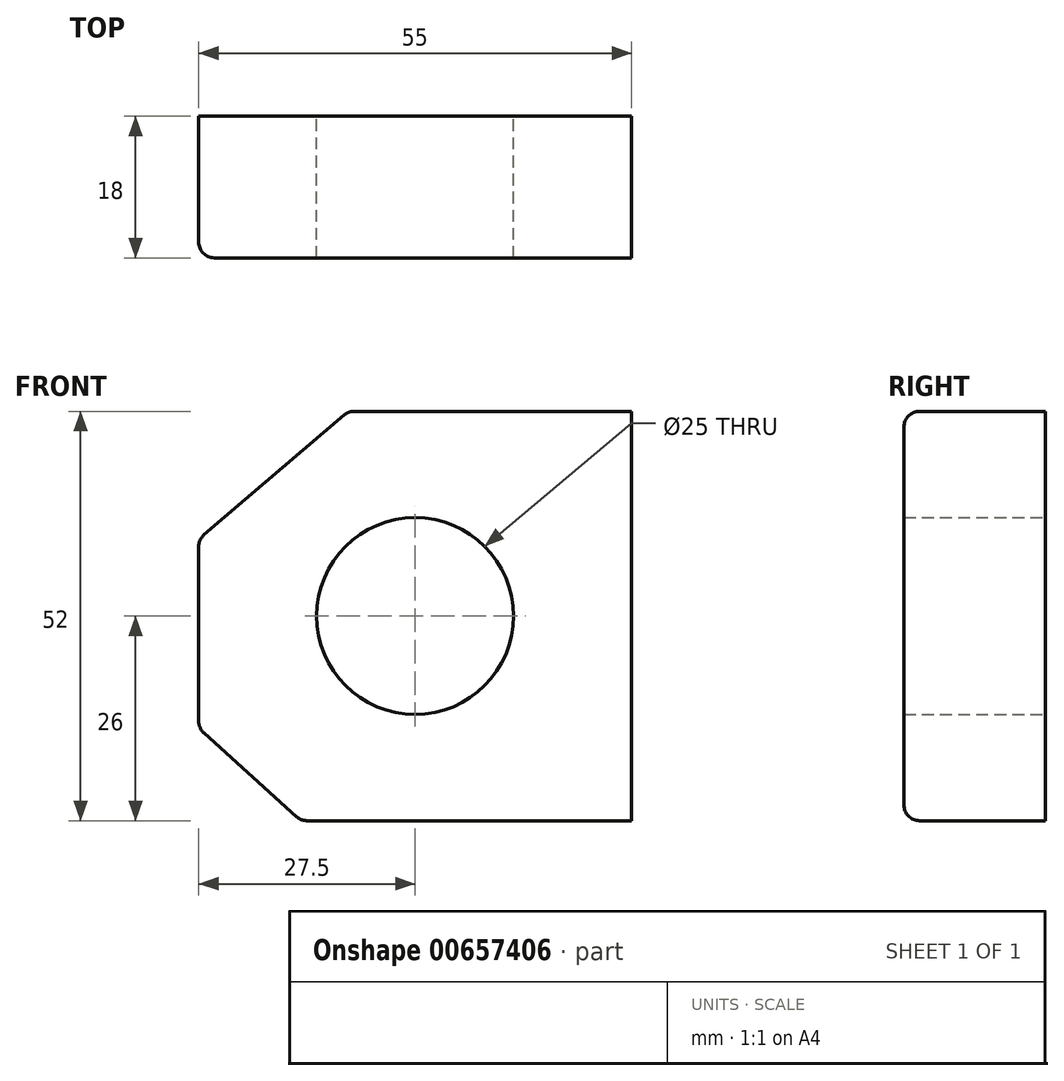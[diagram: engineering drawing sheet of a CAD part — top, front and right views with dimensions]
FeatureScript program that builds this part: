
annotation { "Feature Type Name" : "Feature", "Feature Type Description" : "" }
export const myFeature = defineFeature(function(context is Context, id is Id, definition is map)
    precondition{}
    {
        {
            var Q0;
            Q0=qCreatedBy(makeId("Front.planeOp"),FACE);
            var sketch = newSketch(context, id + "F0", { "sketchPlane" : qUnion([Q0])});
            skLineSegment(sketch, "E0.bottom", {"start": v(27.5, -26) * mm, "end": v(-14.5, -26) * mm});
            skLineSegment(sketch, "E0.top", {"start": v(27.5, 26) * mm, "end": v(-8.5, 26) * mm});
            skLineSegment(sketch, "E0.left", {"start": v(27.5, -26) * mm, "end": v(27.5, 26) * mm});
            skLineSegment(sketch, "E0.right", {"start": v(-27.5, -14.25) * mm, "end": v(-27.5, 9.75) * mm});
            skPoint(sketch, "E0.middle", {"position": v(0, 0) * mm});
            skLineSegment(sketch, "E1", {"start": v(-8.5, 26) * mm, "end": v(-27.5, 9.75) * mm});
            skPoint(sketch, "E2.orphan", {"position": v(-27.5, 26) * mm});
            skLineSegment(sketch, "E3", {"start": v(-27.5, -14.25) * mm, "end": v(-14.5, -26) * mm});
            skPoint(sketch, "E4.orphan", {"position": v(-27.5, -26) * mm});
            skCircle(sketch, "E5", {"center": v(0, 0) * mm, "radius": 12.5 * mm});
            skSolve(sketch);
        }
        {
            var Q0;
            Q0=makeQuery(id+"F0.imprint","IMPRINT",FACE,{"disambiguationData":[TD([[makeQuery(id+"F0.imprint","IMPRINT",EDGE,{"derivedFrom":sQuery(id+"F0.wireOp",EDGE,"E0.bottom")}),-1.0]])]});
            extrude(context, id + "F1", {"entities" : qUnion([Q0]), "endBound" : BoundingType.SYMMETRIC, "depth" : 18 * mm, "offsetDistance" : 25 * mm});
        }
        {
            var Q0;
            Q0=makeQuery(id+"F1.opExtrude","CAP_EDGE",EDGE,{"disambiguationData":[OSD([sQuery(id+"F0.wireOp",EDGE,"E0.top")])],"isStart":false});
            var Q1;
            Q1=makeQuery(id+"F1.opExtrude","CAP_EDGE",EDGE,{"disambiguationData":[OSD([sQuery(id+"F0.wireOp",EDGE,"E1")])],"isStart":false});
            var Q2;
            Q2=makeQuery(id+"F1.opExtrude","CAP_EDGE",EDGE,{"disambiguationData":[OSD([sQuery(id+"F0.wireOp",EDGE,"E0.right")])],"isStart":false});
            var Q3;
            Q3=makeQuery(id+"F1.opExtrude","CAP_EDGE",EDGE,{"disambiguationData":[OSD([sQuery(id+"F0.wireOp",EDGE,"E3")])],"isStart":false});
            var Q4;
            Q4=makeQuery(id+"F1.opExtrude","CAP_EDGE",EDGE,{"disambiguationData":[OSD([sQuery(id+"F0.wireOp",EDGE,"E0.bottom")])],"isStart":false});
            var Q5;
            Q5=makeQuery(id+"F1.opExtrude","SWEPT_EDGE",EDGE,{"disambiguationData":[OSD([sQuery(id+"F0.wireOp",EDGE,"E0.top"),sQuery(id+"F0.wireOp",EDGE,"E1")])]});
            var Q6;
            Q6=makeQuery(id+"F1.opExtrude","SWEPT_EDGE",EDGE,{"disambiguationData":[OSD([sQuery(id+"F0.wireOp",EDGE,"E0.right"),sQuery(id+"F0.wireOp",EDGE,"E1")])]});
            var Q7;
            Q7=makeQuery(id+"F1.opExtrude","SWEPT_EDGE",EDGE,{"disambiguationData":[OSD([sQuery(id+"F0.wireOp",EDGE,"E0.right"),sQuery(id+"F0.wireOp",EDGE,"E3")])]});
            var Q8;
            Q8=makeQuery(id+"F1.opExtrude","SWEPT_EDGE",EDGE,{"disambiguationData":[OSD([sQuery(id+"F0.wireOp",EDGE,"E0.bottom"),sQuery(id+"F0.wireOp",EDGE,"E3")])]});
            fillet(context, id + "F2", {"entities" : qUnion([Q0, Q1, Q2, Q3, Q4, Q5, Q6, Q7, Q8]), "radius" : 2 * mm, "tangentPropagation" : true, "allowEdgeOverflow" : false});
        }
    });
